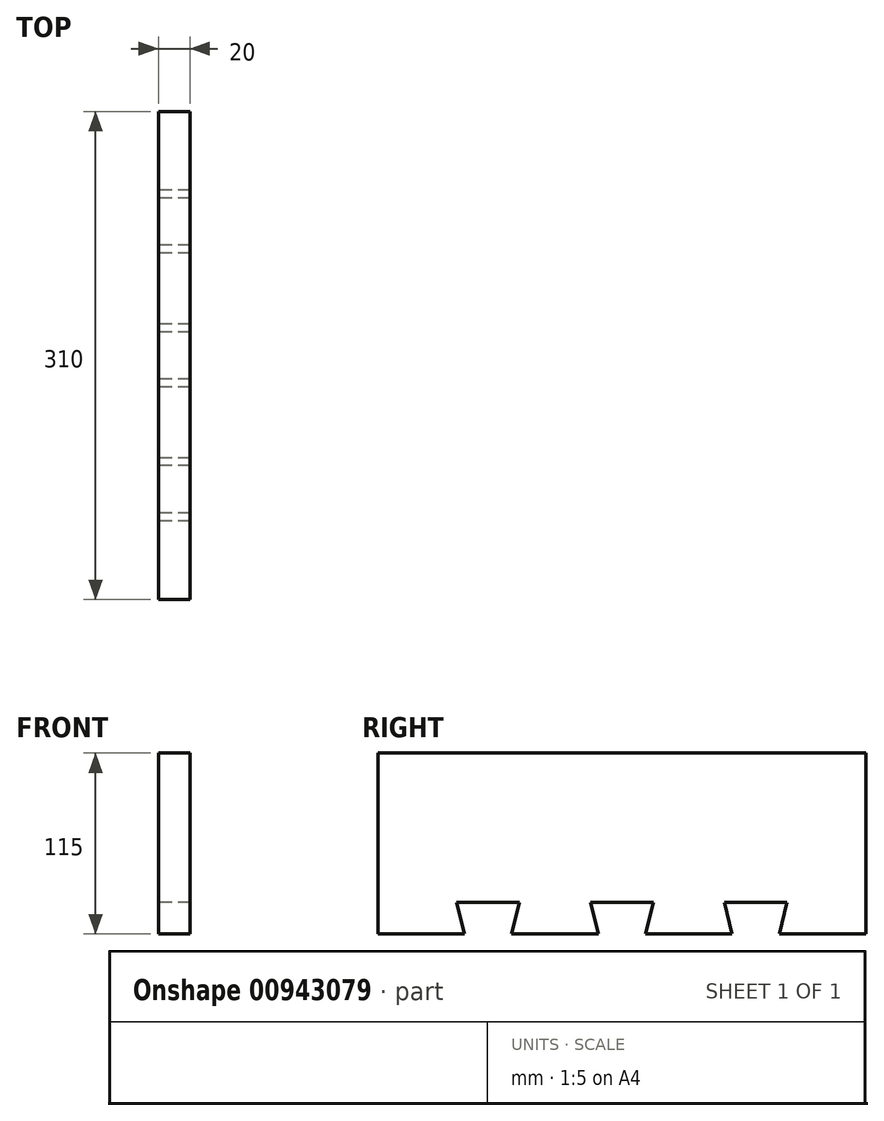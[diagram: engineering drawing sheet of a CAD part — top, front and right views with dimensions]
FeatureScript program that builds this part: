
annotation { "Feature Type Name" : "Feature", "Feature Type Description" : "" }
export const myFeature = defineFeature(function(context is Context, id is Id, definition is map)
    precondition{}
    {
        {
            var Q0;
            Q0=qCreatedBy(makeId("Right.planeOp"),FACE);
            var sketch = newSketch(context, id + "F0", { "sketchPlane" : qUnion([Q0])});
            skLineSegment(sketch, "E0.bottom", {"start": v(-117.47, 54.63) * mm, "end": v(192.53, 54.63) * mm});
            skLineSegment(sketch, "E0.top", {"start": v(-117.47, -60.37) * mm, "end": v(192.53, -60.37) * mm});
            skLineSegment(sketch, "E0.left", {"start": v(-117.47, 54.63) * mm, "end": v(-117.47, -60.37) * mm});
            skLineSegment(sketch, "E0.right", {"start": v(192.53, 54.63) * mm, "end": v(192.53, -60.37) * mm});
            skLineSegment(sketch, "E1.bottom", {"start": v(-62.47, 54.63) * mm, "end": v(-32.47, 54.63) * mm});
            skLineSegment(sketch, "E1.top", {"start": v(-62.47, 79.63) * mm, "end": v(-32.47, 79.63) * mm});
            skLineSegment(sketch, "E1.left", {"start": v(-62.47, 54.63) * mm, "end": v(-62.47, 79.63) * mm});
            skLineSegment(sketch, "E1.right", {"start": v(-32.47, 54.63) * mm, "end": v(-32.47, 79.63) * mm});
            skLineSegment(sketch, "E2.bottom", {"start": v(22.53, 54.63) * mm, "end": v(52.53, 54.63) * mm});
            skLineSegment(sketch, "E2.top", {"start": v(22.53, 79.63) * mm, "end": v(52.53, 79.63) * mm});
            skLineSegment(sketch, "E2.left", {"start": v(22.53, 54.63) * mm, "end": v(22.53, 79.63) * mm});
            skLineSegment(sketch, "E2.right", {"start": v(52.53, 54.63) * mm, "end": v(52.53, 79.63) * mm});
            skLineSegment(sketch, "E3.bottom", {"start": v(107.53, 54.63) * mm, "end": v(137.53, 54.63) * mm});
            skLineSegment(sketch, "E3.top", {"start": v(107.53, 79.63) * mm, "end": v(137.53, 79.63) * mm});
            skLineSegment(sketch, "E3.left", {"start": v(107.53, 54.63) * mm, "end": v(107.53, 79.63) * mm});
            skLineSegment(sketch, "E3.right", {"start": v(137.53, 54.63) * mm, "end": v(137.53, 79.63) * mm});
            skLineSegment(sketch, "E4", {"start": v(-62.47, -60.37) * mm, "end": v(-67.47, -40.37) * mm});
            skLineSegment(sketch, "E5", {"start": v(-67.47, -40.37) * mm, "end": v(-27.47, -40.37) * mm});
            skLineSegment(sketch, "E6", {"start": v(-27.47, -40.37) * mm, "end": v(-32.47, -60.37) * mm});
            skLineSegment(sketch, "E7", {"start": v(22.53, -60.37) * mm, "end": v(17.53, -40.37) * mm});
            skLineSegment(sketch, "E8", {"start": v(17.53, -40.37) * mm, "end": v(57.53, -40.37) * mm});
            skLineSegment(sketch, "E9", {"start": v(57.53, -40.37) * mm, "end": v(52.53, -60.37) * mm});
            skLineSegment(sketch, "E10", {"start": v(107.53, -60.37) * mm, "end": v(102.53, -40.37) * mm});
            skLineSegment(sketch, "E11", {"start": v(102.53, -40.37) * mm, "end": v(142.53, -40.37) * mm});
            skLineSegment(sketch, "E12", {"start": v(142.53, -40.37) * mm, "end": v(137.53, -60.37) * mm});
            skSolve(sketch);
        }
        {
            var Q0;
            {var subQ7=sQuery(id+"F0.wireOp",EDGE,"E0.left");Q0=makeQuery(id+"F0.imprint","IMPRINT",FACE,{"disambiguationData":[TD([[makeQuery(id+"F0.imprint","IMPRINT",EDGE,{"derivedFrom":subQ7}),1.0]])]});}
            var Q1;
            Q1=makeQuery(id+"F0.imprint","IMPRINT",FACE,{"disambiguationData":[TD([[makeQuery(id+"F0.imprint","IMPRINT",EDGE,{"derivedFrom":sQuery(id+"F0.wireOp",EDGE,"E3.bottom")}),1.0]])]});
            var Q2;
            Q2=makeQuery(id+"F0.imprint","IMPRINT",FACE,{"disambiguationData":[TD([[makeQuery(id+"F0.imprint","IMPRINT",EDGE,{"derivedFrom":sQuery(id+"F0.wireOp",EDGE,"E2.bottom")}),1.0]])]});
            var Q3;
            Q3=makeQuery(id+"F0.imprint","IMPRINT",FACE,{"disambiguationData":[TD([[makeQuery(id+"F0.imprint","IMPRINT",EDGE,{"derivedFrom":sQuery(id+"F0.wireOp",EDGE,"E1.bottom")}),1.0]])]});
            extrude(context, id + "F1", {"entities" : qUnion([Q0, Q1, Q2, Q3]), "depth" : 20 * mm, "offsetDistance" : 25 * mm});
        }
    });
